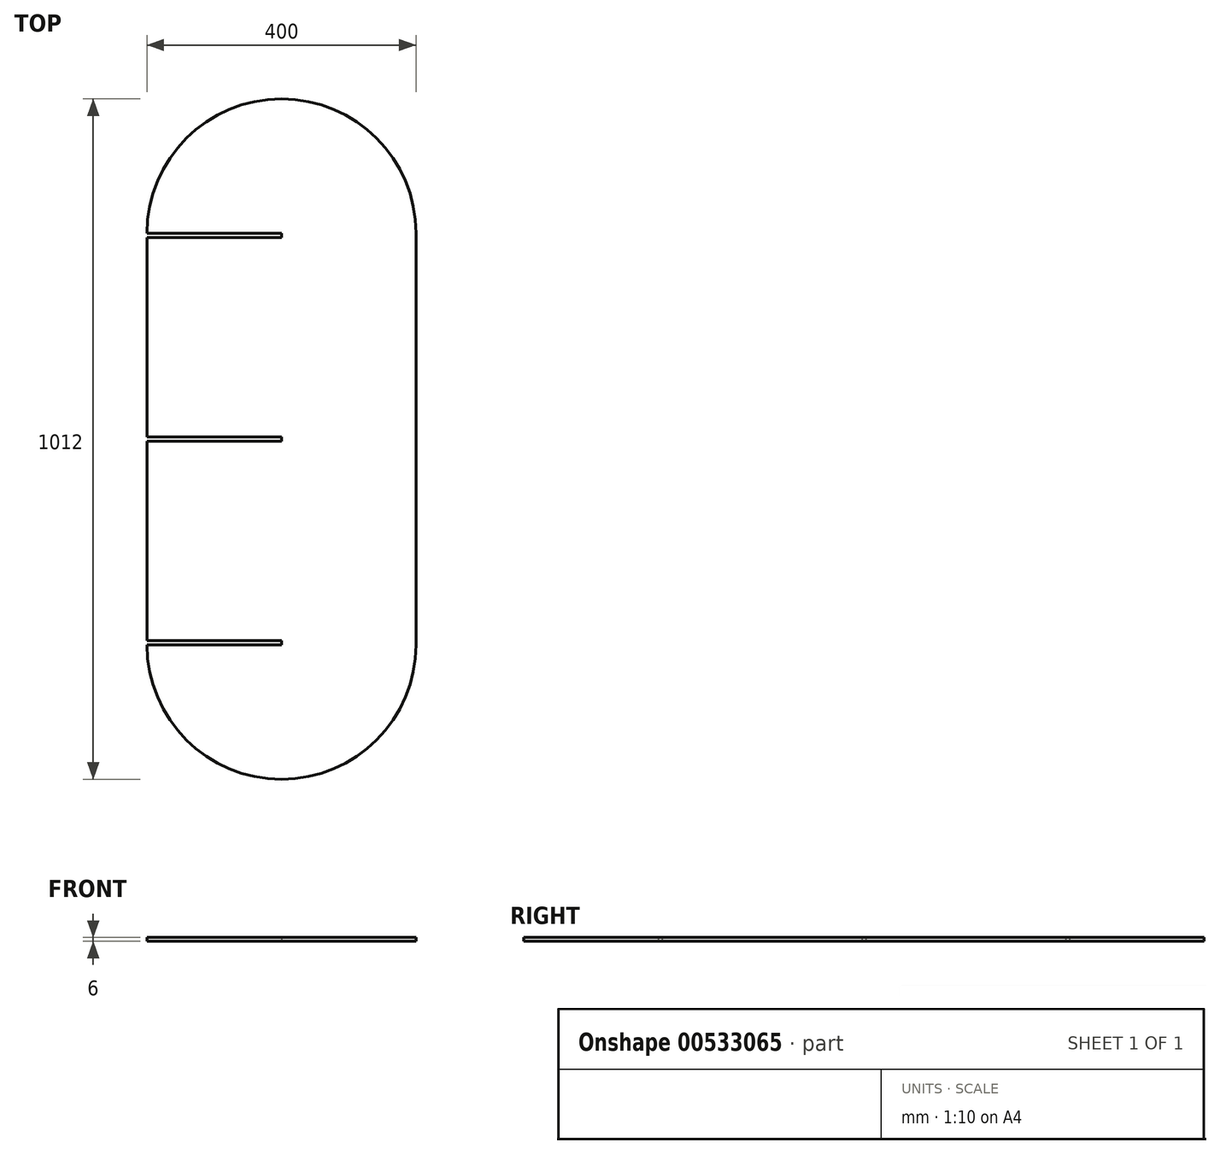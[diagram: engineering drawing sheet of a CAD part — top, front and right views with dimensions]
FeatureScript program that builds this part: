
annotation { "Feature Type Name" : "Feature", "Feature Type Description" : "" }
export const myFeature = defineFeature(function(context is Context, id is Id, definition is map)
    precondition{}
    {
        {
            var Q0;
            Q0=qCreatedBy(makeId("Top.planeOp"),FACE);
            var sketch = newSketch(context, id + "F0", { "sketchPlane" : qUnion([Q0])});
            skLineSegment(sketch, "E0.bottom", {"start": v(-40.1, 606) * mm, "end": v(159.9, 606) * mm});
            skLineSegment(sketch, "E0.top", {"start": v(-40.1, -6) * mm, "end": v(159.9, -6) * mm});
            skLineSegment(sketch, "E0.left", {"start": v(-40.1, 600) * mm, "end": v(-40.1, 303) * mm});
            skLineSegment(sketch, "E0.right", {"start": v(359.9, 606) * mm, "end": v(359.9, -6) * mm});
            skArc(sketch, "E1", {"start": v(359.9, 606) * mm, "mid": v(159.9, 806) * mm, "end": v(-40.1, 606) * mm});
            skArc(sketch, "E2", {"start": v(-40.1, -6) * mm, "mid": v(159.9, -206) * mm, "end": v(359.9, -6) * mm});
            skLineSegment(sketch, "E3.top", {"start": v(-40.1, 600) * mm, "end": v(159.9, 600) * mm});
            skLineSegment(sketch, "E3.right", {"start": v(159.9, 606) * mm, "end": v(159.9, 600) * mm});
            skLineSegment(sketch, "E4.bottom", {"start": v(-40.1, 303) * mm, "end": v(159.9, 303) * mm});
            skLineSegment(sketch, "E4.top", {"start": v(-40.1, 297) * mm, "end": v(159.9, 297) * mm});
            skLineSegment(sketch, "E4.right", {"start": v(159.9, 303) * mm, "end": v(159.9, 297) * mm});
            skLineSegment(sketch, "E5.top", {"start": v(-40.1, 0) * mm, "end": v(159.9, 0) * mm});
            skLineSegment(sketch, "E5.right", {"start": v(159.9, -6) * mm, "end": v(159.9, 0) * mm});
            skLineSegment(sketch, "E6.trimOffspring", {"start": v(-40.1, 297) * mm, "end": v(-40.1, 0) * mm});
            skSolve(sketch);
        }
        {
            var Q0;
            Q0=makeQuery(id+"F0.imprint","IMPRINT",FACE,{"disambiguationData":[TD([[makeQuery(id+"F0.imprint","IMPRINT",EDGE,{"derivedFrom":sQuery(id+"F0.wireOp",EDGE,"E0.left")}),1.0]])]});
            extrude(context, id + "F1", {"entities" : qUnion([Q0]), "depth" : 6 * mm, "offsetDistance" : 25 * mm});
        }
    });
